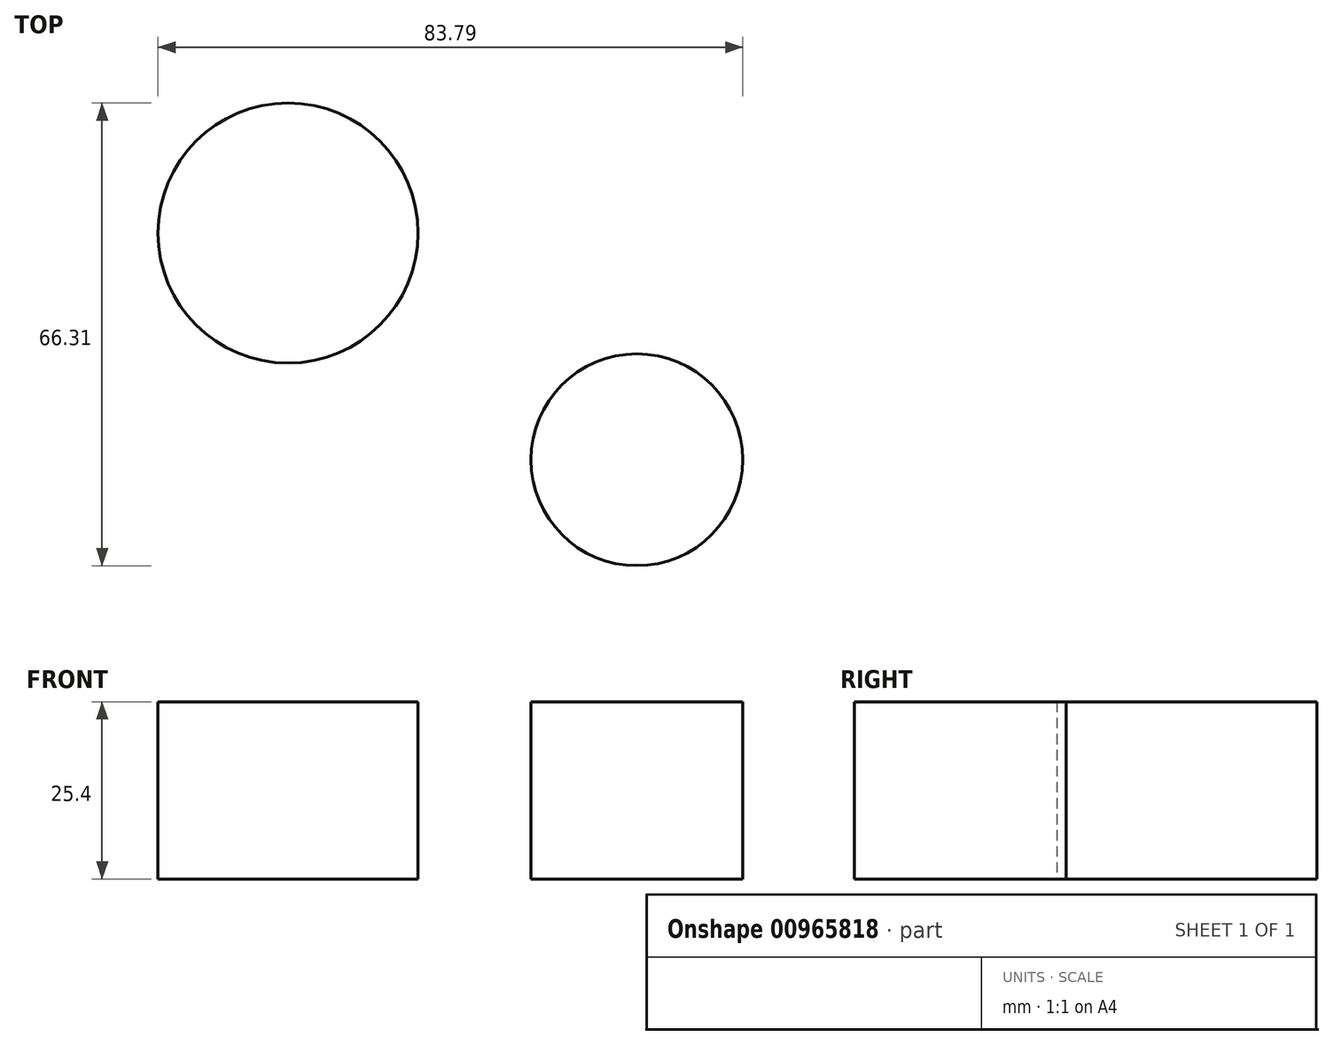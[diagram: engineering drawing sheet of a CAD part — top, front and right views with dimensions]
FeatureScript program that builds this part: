
annotation { "Feature Type Name" : "Feature", "Feature Type Description" : "" }
export const myFeature = defineFeature(function(context is Context, id is Id, definition is map)
    precondition{}
    {
        {
            var Q0;
            Q0=qCreatedBy(makeId("Top.planeOp"),FACE);
            var sketch = newSketch(context, id + "F0", { "sketchPlane" : qUnion([Q0])});
            skCircle(sketch, "E0", {"center": v(36.6, 0) * mm, "radius": 15.18 * mm});
            skCircle(sketch, "E1", {"center": v(-13.39, 32.5) * mm, "radius": 18.64 * mm});
            skPoint(sketch, "E2", {"position": v(31.42, -14.27) * mm});
            skPoint(sketch, "E3", {"position": v(-21.34, 15.64) * mm});
            skPoint(sketch, "E4", {"position": v(23.77, -8.12) * mm});
            skPoint(sketch, "E5", {"position": v(-14.1, 13.87) * mm});
            skPoint(sketch, "E6", {"position": v(0, 13.87) * mm});
            skPoint(sketch, "E7", {"position": v(0, 0) * mm});
            skPoint(sketch, "E8", {"position": v(46.93, -31.87) * mm});
            skPoint(sketch, "E9", {"position": v(-34.02, 72.88) * mm});
            skPoint(sketch, "E10", {"position": v(39.84, -0.33) * mm});
            skPoint(sketch, "E11", {"position": v(4.2, 7.65) * mm});
            skPoint(sketch, "E12", {"position": v(0, -20.16) * mm});
            skPoint(sketch, "E13", {"position": v(30.94, -28.57) * mm});
            skPoint(sketch, "E14", {"position": v(49.11, -35.46) * mm});
            skPoint(sketch, "E15", {"position": v(9.67, 13.87) * mm});
            skSolve(sketch);
        }
        {
            var Q0;
            Q0 = qSketchRegion(id + "F0", true);
            extrude(context, id + "F1", {"entities" : qUnion([Q0]), "depth" : 25.4 * mm, "offsetDistance" : 25.4 * mm});
        }
    });
